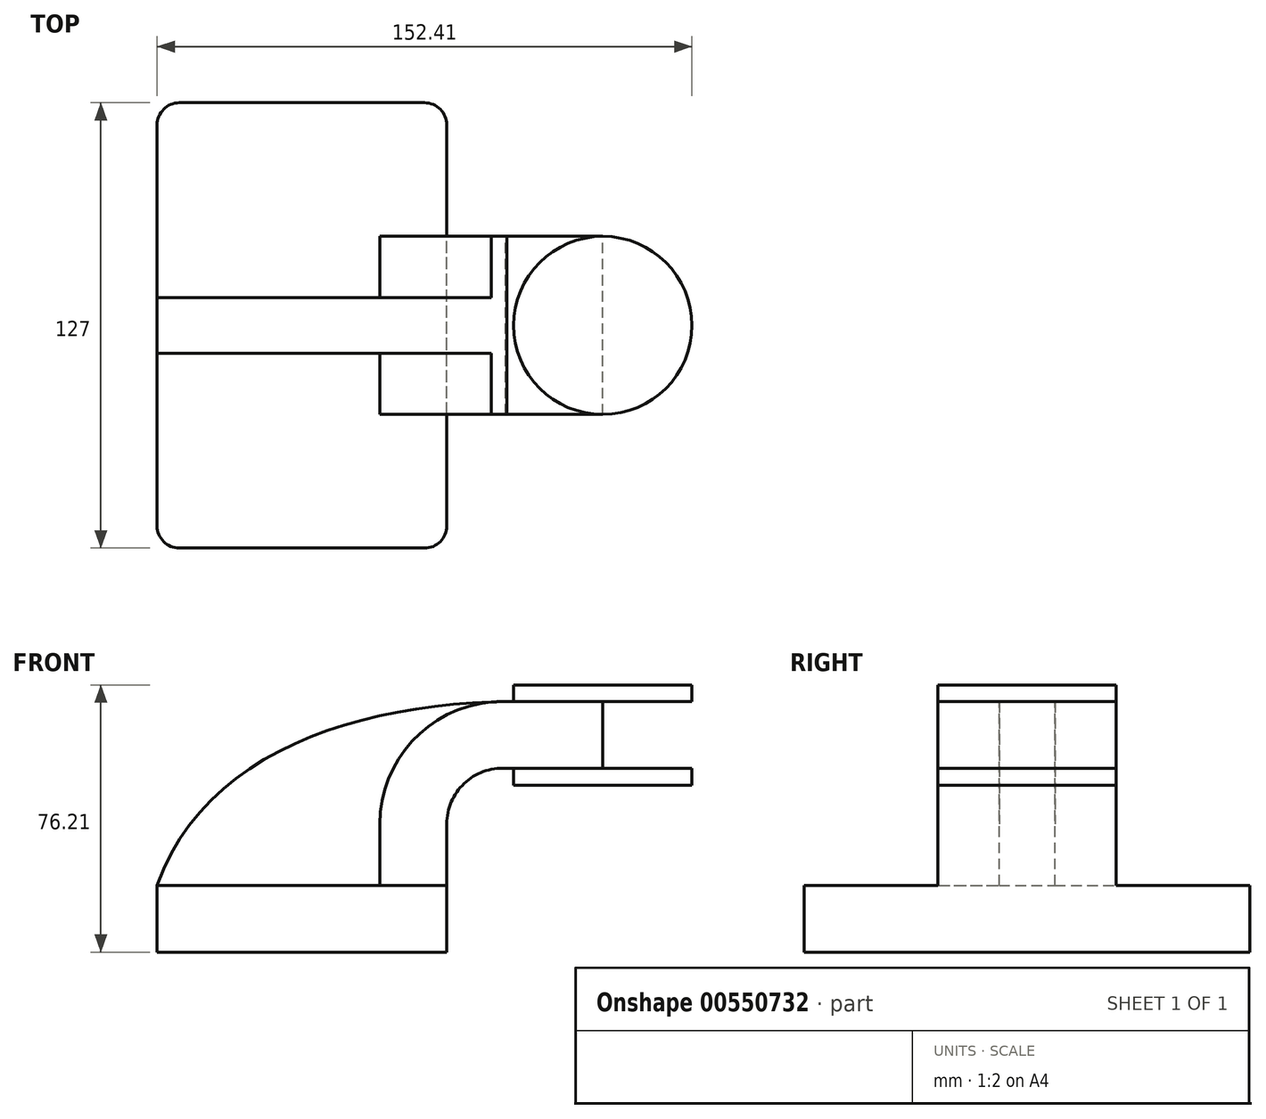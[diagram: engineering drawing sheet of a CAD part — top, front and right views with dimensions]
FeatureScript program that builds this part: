
annotation { "Feature Type Name" : "Feature", "Feature Type Description" : "" }
export const myFeature = defineFeature(function(context is Context, id is Id, definition is map)
    precondition{}
    {
        {
            var Q0;
            Q0=qCreatedBy(makeId("Front.planeOp"),FACE);
            var sketch = newSketch(context, id + "F0", { "sketchPlane" : qUnion([Q0])});
            skLineSegment(sketch, "E0.bottom", {"start": v(-41.28, 9.52) * mm, "end": v(41.28, 9.53) * mm});
            skLineSegment(sketch, "E0.top", {"start": v(-41.28, -9.53) * mm, "end": v(41.28, -9.53) * mm});
            skLineSegment(sketch, "E0.left", {"start": v(-41.28, 9.52) * mm, "end": v(-41.27, -9.53) * mm});
            skLineSegment(sketch, "E0.right", {"start": v(41.28, 9.53) * mm, "end": v(41.28, -9.52) * mm});
            skPoint(sketch, "E0.middle", {"position": v(0, 0) * mm});
            skLineSegment(sketch, "E1.bottom", {"start": v(111.13, 38.1) * mm, "end": v(60.33, 38.1) * mm});
            skLineSegment(sketch, "E1.top", {"start": v(111.13, 66.68) * mm, "end": v(60.33, 66.68) * mm});
            skLineSegment(sketch, "E1.left", {"start": v(111.13, 38.1) * mm, "end": v(111.13, 66.68) * mm});
            skLineSegment(sketch, "E1.right", {"start": v(60.33, 38.1) * mm, "end": v(60.33, 66.68) * mm});
            skPoint(sketch, "E1.middle", {"position": v(85.73, 52.39) * mm});
            skLineSegment(sketch, "E2", {"start": v(41.27, 9.53) * mm, "end": v(41.27, 27.02) * mm});
            skArc(sketch, "E3", {"start": v(41.27, 27.02) * mm, "mid": v(46.23, 38.55) * mm, "end": v(58, 42.88) * mm});
            skLineSegment(sketch, "E4", {"start": v(58, 42.88) * mm, "end": v(111.13, 42.88) * mm});
            skLineSegment(sketch, "E5.0", {"start": v(58.42, 61.93) * mm, "end": v(111.13, 61.93) * mm});
            skArc(sketch, "E5.1", {"start": v(22.22, 27.02) * mm, "mid": v(32.9, 52.16) * mm, "end": v(58.42, 61.93) * mm});
            skLineSegment(sketch, "E5.2", {"start": v(22.23, 9.53) * mm, "end": v(22.23, 27.02) * mm});
            skFitSpline(sketch, "E6", {"points": [v(-41.28, 9.53) * mm, v(58.42, 61.93) * mm], "startDerivative": vector(40.44, 114.01) * mm, "endDerivative": vector(128.9, 2.21) * mm});
            skLineSegment(sketch, "E7", {"start": v(85.73, 52.39) * mm, "end": v(85.73, 38.1) * mm});
            skLineSegment(sketch, "E8", {"start": v(85.73, 38.1) * mm, "end": v(85.73, 66.68) * mm});
            skSolve(sketch);
        }
        {
            var Q0;
            Q0=makeQuery(id+"F0.imprint","IMPRINT",FACE,{"disambiguationData":[TD([[makeQuery(id+"F0.imprint","IMPRINT",EDGE,{"derivedFrom":sQuery(id+"F0.wireOp",EDGE,"E0.top")}),1.0]])]});
            extrude(context, id + "F1", {"entities" : qUnion([Q0]), "endBound" : BoundingType.SYMMETRIC, "depth" : 127 * mm, "offsetDistance" : 25.4 * mm});
        }
        {
            var Q0;
            {var subQ1=sQuery(id+"F0.wireOp",EDGE,"E2");Q0=makeQuery(id+"F0.imprint","IMPRINT",FACE,{"disambiguationData":[TD([[makeQuery(id+"F0.imprint","IMPRINT",EDGE,{"derivedFrom":subQ1}),1.0]])]});}
            extrude(context, id + "F2", {"entities" : qUnion([Q0]), "operationType" : NewBodyOperationType.ADD, "endBound" : BoundingType.SYMMETRIC, "depth" : 50.8 * mm, "offsetDistance" : 25.4 * mm});
        }
        {
            var Q0;
            {var subQ3=sQuery(id+"F0.wireOp",EDGE,"E5.2");Q0=makeQuery(id+"F0.imprint","IMPRINT",FACE,{"disambiguationData":[TD([[makeQuery(id+"F0.imprint","IMPRINT",EDGE,{"derivedFrom":subQ3}),1.0]])]});}
            extrude(context, id + "F3", {"entities" : qUnion([Q0]), "operationType" : NewBodyOperationType.ADD, "endBound" : BoundingType.SYMMETRIC, "depth" : 15.88 * mm, "offsetDistance" : 25.4 * mm});
        }
        {
            var Q0;
            Q0=makeQuery(id+"F2.opExtrude","SWEPT_FACE",FACE,{"disambiguationData":[OSD([sQuery(id+"F0.wireOp",EDGE,"E1.right")])]});
            extrude(context, id + "F4", {"entities" : qUnion([Q0]), "operationType" : NewBodyOperationType.ADD, "depth" : 25.4 * mm, "offsetDistance" : 25.4 * mm});
        }
        {
            var Q0;
            {var subQ0=sQuery(id+"F0.wireOp",EDGE,"E1.left");var subQ1=sQuery(id+"F0.wireOp",EDGE,"E1.top");var subQ2=makeQuery(id+"F0.imprint","INTERSECT",VERTEX,{"derivedFrom":[subQ1,subQ0]});Q0=makeQuery(id+"F0.imprint","IMPRINT",FACE,{"disambiguationData":[TD([[makeQuery(id+"F0.imprint","IMPRINT",EDGE,{"disambiguationData":[TD([[subQ2,-1.0]])],"derivedFrom":subQ1}),1.0]])]});}
            var Q1;
            {var subQ3=sQuery(id+"F0.wireOp",EDGE,"E8");var subQ5=makeQuery(id+"F0.imprint","IMPRINT",VERTEX,{"derivedFrom":subQ3});Q1=makeQuery(id+"F0.imprint","IMPRINT",FACE,{"disambiguationData":[TD([[makeQuery(id+"F0.imprint","IMPRINT",EDGE,{"disambiguationData":[TD([[subQ5,1.0]])],"derivedFrom":subQ3}),-1.0]])]});}
            var Q2;
            {var subQ0=sQuery(id+"F0.wireOp",EDGE,"E1.left");var subQ1=sQuery(id+"F0.wireOp",EDGE,"E1.bottom");var subQ2=makeQuery(id+"F0.imprint","INTERSECT",VERTEX,{"derivedFrom":[subQ1,subQ0]});Q2=makeQuery(id+"F0.imprint","IMPRINT",FACE,{"disambiguationData":[TD([[makeQuery(id+"F0.imprint","IMPRINT",EDGE,{"disambiguationData":[TD([[subQ2,-1.0]])],"derivedFrom":subQ1}),-1.0]])]});}
            var Q3;
            Q3=sQuery(id+"F0.wireOp",EDGE,"E8");
            revolve(context, id + "F5", {"operationType" : NewBodyOperationType.ADD, "entities" : qUnion([Q0, Q1, Q2]), "axis" : qUnion([Q3]), "revolveType" : RevolveType.FULL});
        }
        {
            var Q0;
            Q0=makeQuery(id+"F1.opExtrude","CAP_EDGE",EDGE,{"disambiguationData":[OSD([sQuery(id+"F0.wireOp",EDGE,"E0.right")])],"isStart":false});
            var Q1;
            Q1=makeQuery(id+"F1.opExtrude","CAP_EDGE",EDGE,{"disambiguationData":[OSD([sQuery(id+"F0.wireOp",EDGE,"E0.left")])],"isStart":false});
            var Q2;
            Q2=makeQuery(id+"F1.opExtrude","CAP_EDGE",EDGE,{"disambiguationData":[OSD([sQuery(id+"F0.wireOp",EDGE,"E0.right")])],"isStart":true});
            var Q3;
            Q3=makeQuery(id+"F1.opExtrude","CAP_EDGE",EDGE,{"disambiguationData":[OSD([sQuery(id+"F0.wireOp",EDGE,"E0.left")])],"isStart":true});
            fillet(context, id + "F6", {"entities" : qUnion([Q0, Q1, Q2, Q3]), "radius" : 6.35 * mm, "tangentPropagation" : true, "allowEdgeOverflow" : false});
        }
    });
